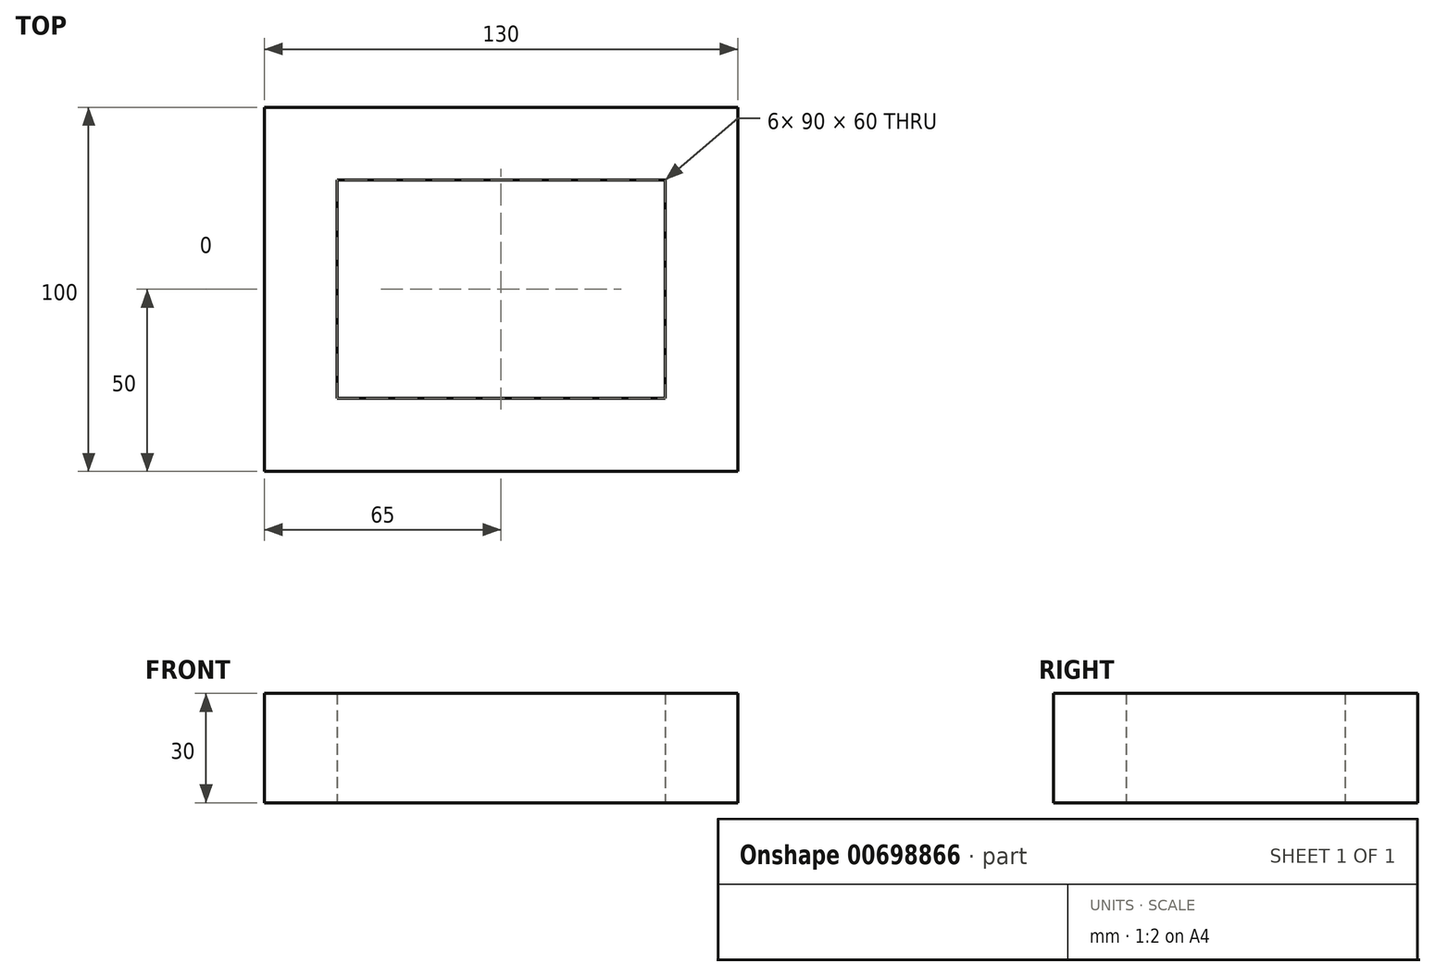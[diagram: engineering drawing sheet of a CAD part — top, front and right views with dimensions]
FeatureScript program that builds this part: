
annotation { "Feature Type Name" : "Feature", "Feature Type Description" : "" }
export const myFeature = defineFeature(function(context is Context, id is Id, definition is map)
    precondition{}
    {
        {
            var Q0;
            Q0=qCreatedBy(makeId("Top.planeOp"),FACE);
            var sketch = newSketch(context, id + "F0", { "sketchPlane" : qUnion([Q0])});
            skLineSegment(sketch, "E0.bottom", {"start": v(0, 0) * mm, "end": v(-90, 0) * mm});
            skLineSegment(sketch, "E0.top", {"start": v(0, 60) * mm, "end": v(-90, 60) * mm});
            skLineSegment(sketch, "E0.left", {"start": v(0, 0) * mm, "end": v(0, 60) * mm});
            skLineSegment(sketch, "E0.right", {"start": v(-90, 0) * mm, "end": v(-90, 60) * mm});
            skLineSegment(sketch, "E1.0", {"start": v(20, 80) * mm, "end": v(-110, 80) * mm});
            skLineSegment(sketch, "E1.1", {"start": v(20, -20) * mm, "end": v(20, 80) * mm});
            skLineSegment(sketch, "E1.2", {"start": v(20, -20) * mm, "end": v(-110, -20) * mm});
            skLineSegment(sketch, "E1.3", {"start": v(-110, -20) * mm, "end": v(-110, 80) * mm});
            skSolve(sketch);
        }
        {
            var Q0;
            Q0 = qSketchRegion(id + "F0", true);
            extrude(context, id + "F1", {"entities" : qUnion([Q0]), "depth" : 30 * mm, "offsetDistance" : 25 * mm});
        }
    });
